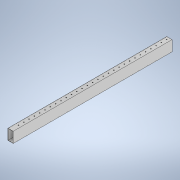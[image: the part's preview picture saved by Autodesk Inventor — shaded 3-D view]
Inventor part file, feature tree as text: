
AUTODESK INVENTOR PART (.ipt)
format: ipt  version: 2020 (Build 240168000, 168)  size: 184,832 bytes
history: native  units: in
note: dims shown in document units (in); Inventor stores cm internally (conversion verified against a paired STEP export)
features: extrude x2, sketch x2
ambient origin geometry x8: Origin, YZ Plane, XZ Plane, XY Plane, X Axis, Y Axis, Z Axis, Center Point
bodies: Solid1 (feature_tree)
feature tree (4):
  extrude  "Extrusion1"  Depth=2.0in
  extrude  "Extrusion2"  Depth=30.0in TaperAngle=0.0deg
  sketch  "Sketch1"  dims[d0=1.0in d1=2.0in]
  sketch  "Sketch2"  dims[d2=0.04in d3=30.0in d4=0.0in d5=0.1562in d6=0.5in d7=0.5in d8=12.9921in d10=1.0in d11=0.3937in d13=1.0in d15=22.0in d16=0.0in]
